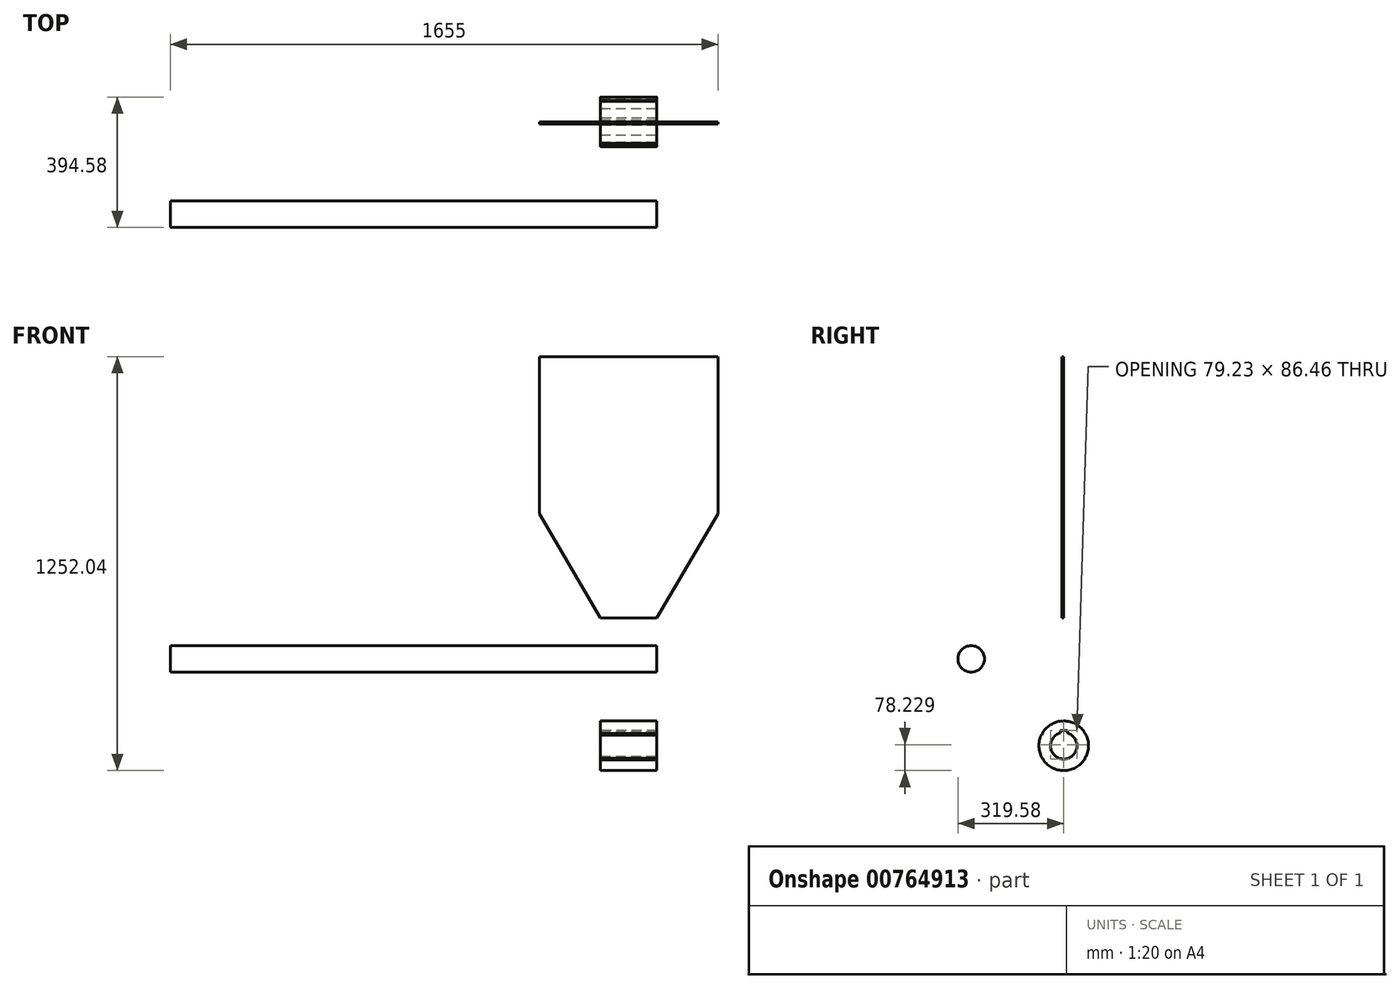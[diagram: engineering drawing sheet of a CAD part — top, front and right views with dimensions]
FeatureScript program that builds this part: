
annotation { "Feature Type Name" : "Feature", "Feature Type Description" : "" }
export const myFeature = defineFeature(function(context is Context, id is Id, definition is map)
    precondition{}
    {
        {
            var Q0;
            Q0=qCreatedBy(makeId("Front.planeOp"),FACE);
            var sketch = newSketch(context, id + "F0", { "sketchPlane" : qUnion([Q0])});
            skLineSegment(sketch, "E0", {"start": v(-170, 387.04) * mm, "end": v(-355, 702.04) * mm});
            skLineSegment(sketch, "E1", {"start": v(-355, 702.04) * mm, "end": v(-355, 1177.04) * mm});
            skLineSegment(sketch, "E2", {"start": v(-355, 1177.04) * mm, "end": v(185, 1177.04) * mm});
            skLineSegment(sketch, "E3", {"start": v(185, 1177.04) * mm, "end": v(185, 702.04) * mm});
            skLineSegment(sketch, "E4", {"start": v(185, 702.04) * mm, "end": v(0, 387.04) * mm});
            skLineSegment(sketch, "E5", {"start": v(0, 387.04) * mm, "end": v(-170, 387.04) * mm});
            skSolve(sketch);
        }
        {
            var Q0;
            Q0=makeQuery(id+"F0.imprint","IMPRINT",FACE,{"disambiguationData":[TD([[makeQuery(id+"F0.imprint","IMPRINT",EDGE,{"derivedFrom":sQuery(id+"F0.wireOp",EDGE,"E0")}),-1.0]])]});
            extrude(context, id + "F1", {"entities" : qUnion([Q0]), "depth" : 6 * mm, "offsetDistance" : 25 * mm});
        }
        {
            var Q0;
            Q0=qCreatedBy(makeId("Right.planeOp"),FACE);
            var sketch = newSketch(context, id + "F2", { "sketchPlane" : qUnion([Q0])});
            skCircle(sketch, "E6", {"center": v(0, 0) * mm, "radius": 75 * mm});
            skCircle(sketch, "E7", {"center": v(0, 0) * mm, "radius": 40 * mm});
            skLineSegment(sketch, "E8", {"start": v(0, 75) * mm, "end": v(0, 74) * mm});
            skLineSegment(sketch, "E9", {"start": v(0, 74) * mm, "end": v(-6, 74) * mm});
            skLineSegment(sketch, "E10", {"start": v(-6, 74) * mm, "end": v(-6, 74.76) * mm});
            skLineSegment(sketch, "E11.1.0", {"start": v(-64.95, 37.5) * mm, "end": v(-64.09, 37) * mm});
            skLineSegment(sketch, "E11.1.1", {"start": v(-64.09, 37) * mm, "end": v(-67.09, 31.8) * mm});
            skLineSegment(sketch, "E11.1.2", {"start": v(-67.09, 31.8) * mm, "end": v(-67.74, 32.18) * mm});
            skLineSegment(sketch, "E11.2.0", {"start": v(-64.95, -37.5) * mm, "end": v(-64.09, -37) * mm});
            skLineSegment(sketch, "E11.2.1", {"start": v(-64.09, -37) * mm, "end": v(-61.09, -42.2) * mm});
            skLineSegment(sketch, "E11.2.2", {"start": v(-61.09, -42.2) * mm, "end": v(-61.74, -42.58) * mm});
            skLineSegment(sketch, "E11.3.0", {"start": v(0, -75) * mm, "end": v(0, -74) * mm});
            skLineSegment(sketch, "E11.3.1", {"start": v(0, -74) * mm, "end": v(6, -74) * mm});
            skLineSegment(sketch, "E11.3.2", {"start": v(6, -74) * mm, "end": v(6, -74.76) * mm});
            skLineSegment(sketch, "E11.4.0", {"start": v(64.95, -37.5) * mm, "end": v(64.09, -37) * mm});
            skLineSegment(sketch, "E11.4.1", {"start": v(64.09, -37) * mm, "end": v(67.09, -31.8) * mm});
            skLineSegment(sketch, "E11.4.2", {"start": v(67.09, -31.8) * mm, "end": v(67.74, -32.18) * mm});
            skLineSegment(sketch, "E11.5.0", {"start": v(64.95, 37.5) * mm, "end": v(64.09, 37) * mm});
            skLineSegment(sketch, "E11.5.1", {"start": v(64.09, 37) * mm, "end": v(61.09, 42.2) * mm});
            skLineSegment(sketch, "E11.5.2", {"start": v(61.09, 42.2) * mm, "end": v(61.74, 42.58) * mm});
            skSolve(sketch);
        }
        {
            var Q0;
            Q0=makeQuery(id+"F2.imprint","IMPRINT",FACE,{"disambiguationData":[TD([[makeQuery(id+"F2.imprint","IMPRINT",EDGE,{"derivedFrom":sQuery(id+"F2.wireOp",EDGE,"E6")}),1.0]])]});
            extrude(context, id + "F3", {"entities" : qUnion([Q0]), "oppositeDirection" : true, "depth" : 170 * mm, "offsetDistance" : 25 * mm});
        }
        {
            var Q0;
            Q0=makeQuery(id+"F3.opExtrude","CAP_FACE",FACE,{"disambiguationData":[OSD([sQuery(id+"F2.wireOp",EDGE,"E6"),sQuery(id+"F2.wireOp",EDGE,"E7")])],"isStart":false});
            var sketch = newSketch(context, id + "F4", { "sketchPlane" : qUnion([Q0])});
            skLineSegment(sketch, "E12", {"start": v(-11, 38.46) * mm, "end": v(-11, 46.46) * mm});
            skLineSegment(sketch, "E13", {"start": v(-11, 46.46) * mm, "end": v(11, 46.46) * mm});
            skLineSegment(sketch, "E14", {"start": v(11, 46.46) * mm, "end": v(11, 38.46) * mm});
            skSolve(sketch);
        }
        {
            var Q0;
            {var subQ0=sQuery(id+"F4.wireOp",EDGE,"E12");Q0=makeQuery(id+"F4.imprint","IMPRINT",FACE,{"disambiguationData":[TD([[makeQuery(id+"F4.imprint","IMPRINT",EDGE,{"derivedFrom":subQ0}),-1.0]])]});}
            extrude(context, id + "F5", {"entities" : qUnion([Q0]), "operationType" : NewBodyOperationType.REMOVE, "oppositeDirection" : true, "depth" : 170 * mm, "offsetDistance" : 25 * mm});
        }
        {
            var Q0;
            Q0=qCreatedBy(makeId("Right.planeOp"),FACE);
            var sketch = newSketch(context, id + "F6", { "sketchPlane" : qUnion([Q0])});
            skCircle(sketch, "E15", {"center": v(-279.58, 262.67) * mm, "radius": 40 * mm});
            skSolve(sketch);
        }
        {
            var Q0;
            Q0 = qSketchRegion(id + "F6", true);
            var Q1;
            Q1=makeQuery(id+"F6.imprint","IMPRINT",FACE,{"disambiguationData":[TD([[makeQuery(id+"F6.imprint","IMPRINT",EDGE,{"derivedFrom":sQuery(id+"F6.wireOp",EDGE,"E15")}),1.0]])]});
            extrude(context, id + "F7", {"entities" : qUnion([Q0, Q1]), "oppositeDirection" : true, "depth" : 1470 * mm, "offsetDistance" : 25 * mm});
        }
    });
